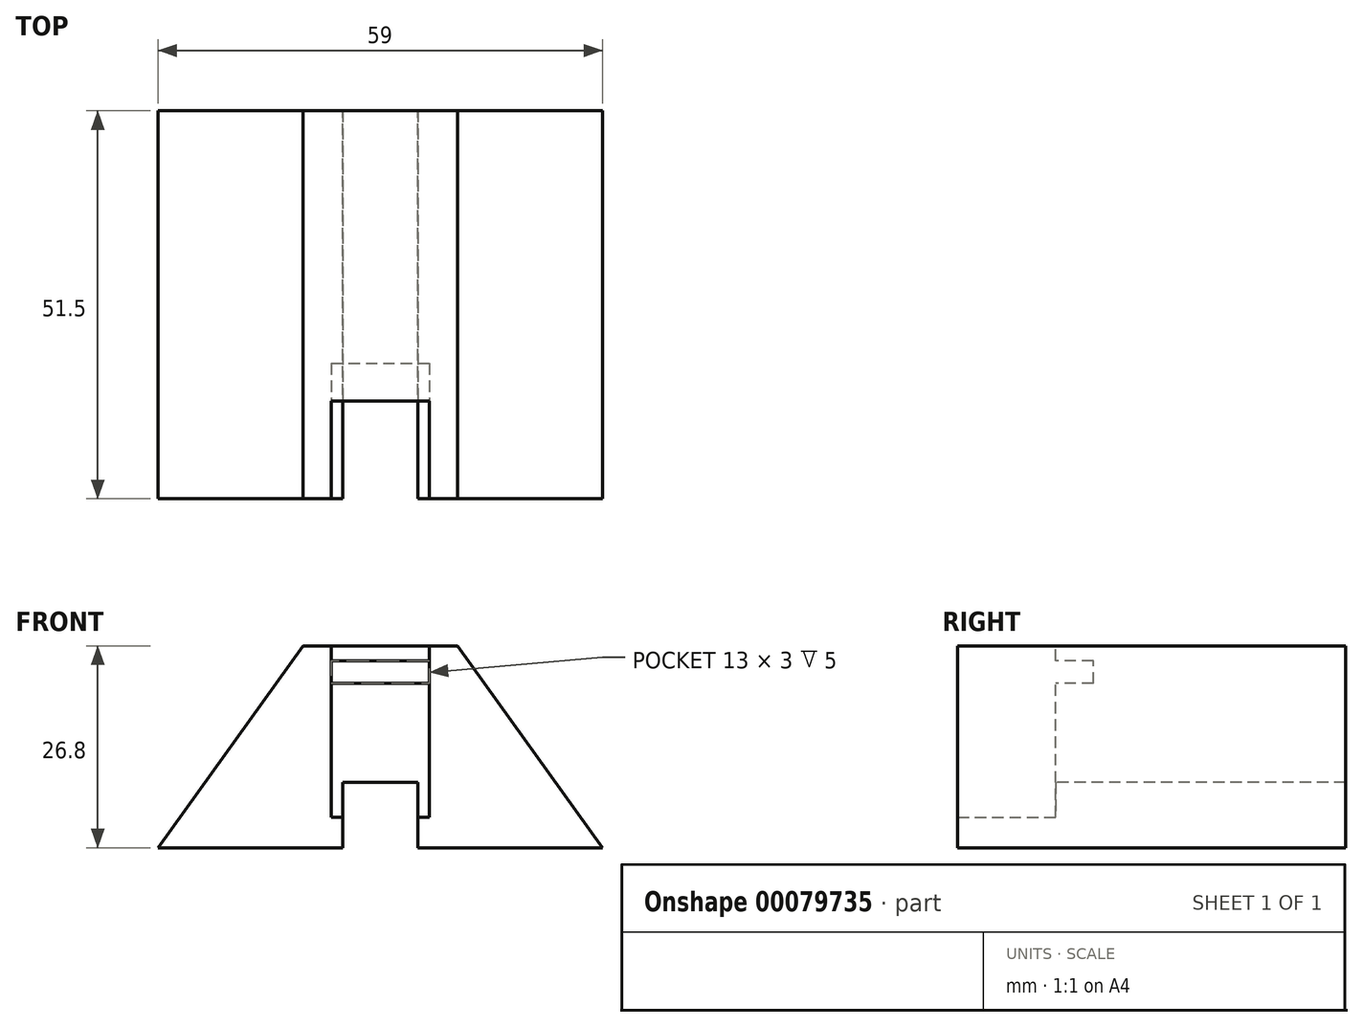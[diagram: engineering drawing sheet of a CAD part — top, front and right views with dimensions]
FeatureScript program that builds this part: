
annotation { "Feature Type Name" : "Feature", "Feature Type Description" : "" }
export const myFeature = defineFeature(function(context is Context, id is Id, definition is map)
    precondition{}
    {
        {
            var Q0;
            Q0=qCreatedBy(makeId("Top.planeOp"),FACE);
            var sketch = newSketch(context, id + "F0", { "sketchPlane" : qUnion([Q0])});
            skLineSegment(sketch, "E0.bottom", {"start": v(29.5, 25.75) * mm, "end": v(-29.5, 25.75) * mm});
            skLineSegment(sketch, "E0.top", {"start": v(29.5, -25.75) * mm, "end": v(-29.5, -25.75) * mm});
            skLineSegment(sketch, "E0.left", {"start": v(29.5, 25.75) * mm, "end": v(29.5, -25.75) * mm});
            skLineSegment(sketch, "E0.right", {"start": v(-29.5, 25.75) * mm, "end": v(-29.5, -25.75) * mm});
            skPoint(sketch, "E0.middle", {"position": v(0, 0) * mm});
            skLineSegment(sketch, "E1", {"start": v(-10.25, 25.75) * mm, "end": v(-10.25, -25.75) * mm});
            skLineSegment(sketch, "E2", {"start": v(10.25, 25.75) * mm, "end": v(10.25, -25.75) * mm});
            skSolve(sketch);
        }
        {
            var Q0;
            Q0 = qSketchRegion(id + "F0", true);
            extrude(context, id + "F1", {"entities" : qUnion([Q0]), "depth" : 26.8 * mm});
        }
        {
            var Q0;
            Q0=makeQuery(id+"F1.opExtrude","CAP_FACE",FACE,{"disambiguationData":[OSD([sQuery(id+"F0.wireOp",EDGE,"E0.bottom"),sQuery(id+"F0.wireOp",EDGE,"E0.top"),sQuery(id+"F0.wireOp",EDGE,"E0.left"),sQuery(id+"F0.wireOp",EDGE,"E0.right")])],"isStart":false});
            var sketch = newSketch(context, id + "F2", { "sketchPlane" : qUnion([Q0])});
            skLineSegment(sketch, "E3.bottom", {"start": v(-6.5, -12.75) * mm, "end": v(6.5, -12.75) * mm});
            skLineSegment(sketch, "E3.top", {"start": v(-6.5, -25.75) * mm, "end": v(6.5, -25.75) * mm});
            skLineSegment(sketch, "E3.left", {"start": v(-6.5, -12.75) * mm, "end": v(-6.5, -25.75) * mm});
            skLineSegment(sketch, "E3.right", {"start": v(6.5, -12.75) * mm, "end": v(6.5, -25.75) * mm});
            skSolve(sketch);
        }
        {
            var Q0;
            Q0 = qSketchRegion(id + "F2", true);
            extrude(context, id + "F3", {"entities" : qUnion([Q0]), "operationType" : NewBodyOperationType.REMOVE, "oppositeDirection" : true, "depth" : 26.8 * mm});
        }
        {
            var Q0;
            {var subQ0=sQuery(id+"F0.wireOp",EDGE,"E1");Q0=makeQuery(id+"F0.imprint","IMPRINT",FACE,{"disambiguationData":[TD([[makeQuery(id+"F0.imprint","IMPRINT",EDGE,{"derivedFrom":subQ0}),1.0]])]});}
            var sketch = newSketch(context, id + "F4", { "sketchPlane" : qUnion([Q0])});
            skLineSegment(sketch, "E4.bottom", {"start": v(-6.5, -25.75) * mm, "end": v(-5, -25.75) * mm});
            skLineSegment(sketch, "E4.top", {"start": v(-6.5, -12.75) * mm, "end": v(-5, -12.75) * mm});
            skLineSegment(sketch, "E4.left", {"start": v(-6.5, -25.75) * mm, "end": v(-6.5, -12.75) * mm});
            skLineSegment(sketch, "E4.right", {"start": v(-5, -25.75) * mm, "end": v(-5, -12.75) * mm});
            skLineSegment(sketch, "E5.bottom", {"start": v(5, -25.75) * mm, "end": v(6.5, -25.75) * mm});
            skLineSegment(sketch, "E5.top", {"start": v(5, -12.75) * mm, "end": v(6.5, -12.75) * mm});
            skLineSegment(sketch, "E5.left", {"start": v(5, -25.75) * mm, "end": v(5, -12.75) * mm});
            skLineSegment(sketch, "E5.right", {"start": v(6.5, -25.75) * mm, "end": v(6.5, -12.75) * mm});
            skSolve(sketch);
        }
        {
            var Q0;
            Q0 = qSketchRegion(id + "F4", true);
            extrude(context, id + "F5", {"entities" : qUnion([Q0]), "operationType" : NewBodyOperationType.ADD, "depth" : 4.05 * mm});
        }
        {
            var Q0;
            {var subQ0=sQuery(id+"F0.wireOp",EDGE,"E0.right");var subQ2=sQuery(id+"F0.wireOp",EDGE,"E0.top");Q0=makeQuery(id+"F5.boolean.opBoolean","MERGE",FACE,{"derivedFrom":[makeQuery(id+"F3.boolean.opBoolean","SPLIT",FACE,{"disambiguationData":[TD([makeQuery(id+"F1.opExtrude","SWEPT_FACE",FACE,{"disambiguationData":[OSD([subQ0])]})])],"derivedFrom":makeQuery(id+"F1.opExtrude","SWEPT_FACE",FACE,{"disambiguationData":[OSD([subQ2])]})}),makeQuery(id+"F5.opExtrude","SWEPT_FACE",FACE,{"disambiguationData":[OSD([sQuery(id+"F4.wireOp",EDGE,"E4.bottom")])]})]});}
            var sketch = newSketch(context, id + "F6", { "sketchPlane" : qUnion([Q0])});
            skLineSegment(sketch, "E6", {"start": v(-29.5, 0) * mm, "end": v(-10.24, 26.8) * mm});
            skLineSegment(sketch, "E7", {"start": v(-10.24, 26.8) * mm, "end": v(-29.5, 26.8) * mm});
            skLineSegment(sketch, "E8", {"start": v(-29.5, 26.8) * mm, "end": v(-29.5, 0) * mm});
            skLineSegment(sketch, "E9", {"start": v(29.5, 0) * mm, "end": v(10.24, 26.8) * mm});
            skLineSegment(sketch, "E10", {"start": v(10.24, 26.8) * mm, "end": v(29.5, 26.8) * mm});
            skLineSegment(sketch, "E11", {"start": v(29.5, 26.8) * mm, "end": v(29.5, 0) * mm});
            skSolve(sketch);
        }
        {
            var Q0;
            Q0 = qSketchRegion(id + "F6", true);
            extrude(context, id + "F7", {"entities" : qUnion([Q0]), "operationType" : NewBodyOperationType.REMOVE, "endBound" : BoundingType.THROUGH_ALL, "oppositeDirection" : true, "depth" : 25 * mm});
        }
        {
            var Q0;
            Q0=makeQuery(id+"F3.boolean.opBoolean","COPY",FACE,{"derivedFrom":makeQuery(id+"F3.opExtrude","SWEPT_FACE",FACE,{"disambiguationData":[OSD([sQuery(id+"F2.wireOp",EDGE,"E3.bottom")])]})});
            var sketch = newSketch(context, id + "F8", { "sketchPlane" : qUnion([Q0])});
            skLineSegment(sketch, "E12.bottom", {"start": v(-5, 8.67) * mm, "end": v(5, 8.67) * mm});
            skLineSegment(sketch, "E12.top", {"start": v(-5, 0) * mm, "end": v(5, 0) * mm});
            skLineSegment(sketch, "E12.left", {"start": v(-5, 8.67) * mm, "end": v(-5, 0) * mm});
            skLineSegment(sketch, "E12.right", {"start": v(5, 8.67) * mm, "end": v(5, 0) * mm});
            skSolve(sketch);
        }
        {
            var Q0;
            Q0 = qSketchRegion(id + "F8", true);
            extrude(context, id + "F9", {"entities" : qUnion([Q0]), "operationType" : NewBodyOperationType.REMOVE, "endBound" : BoundingType.THROUGH_ALL, "oppositeDirection" : true, "depth" : 25 * mm});
        }
        {
            var Q0;
            Q0=makeQuery(id+"F3.boolean.opBoolean","COPY",FACE,{"derivedFrom":makeQuery(id+"F3.opExtrude","SWEPT_FACE",FACE,{"disambiguationData":[OSD([sQuery(id+"F2.wireOp",EDGE,"E3.bottom")])]})});
            var sketch = newSketch(context, id + "F10", { "sketchPlane" : qUnion([Q0])});
            skLineSegment(sketch, "E13.bottom", {"start": v(-6.5, 24.8) * mm, "end": v(6.5, 24.8) * mm});
            skLineSegment(sketch, "E13.top", {"start": v(-6.5, 21.8) * mm, "end": v(6.5, 21.8) * mm});
            skLineSegment(sketch, "E13.left", {"start": v(-6.5, 24.8) * mm, "end": v(-6.5, 21.8) * mm});
            skLineSegment(sketch, "E13.right", {"start": v(6.5, 24.8) * mm, "end": v(6.5, 21.8) * mm});
            skSolve(sketch);
        }
        {
            var Q0;
            Q0 = qSketchRegion(id + "F10", true);
            extrude(context, id + "F11", {"entities" : qUnion([Q0]), "operationType" : NewBodyOperationType.REMOVE, "oppositeDirection" : true, "depth" : 5 * mm});
        }
    });
